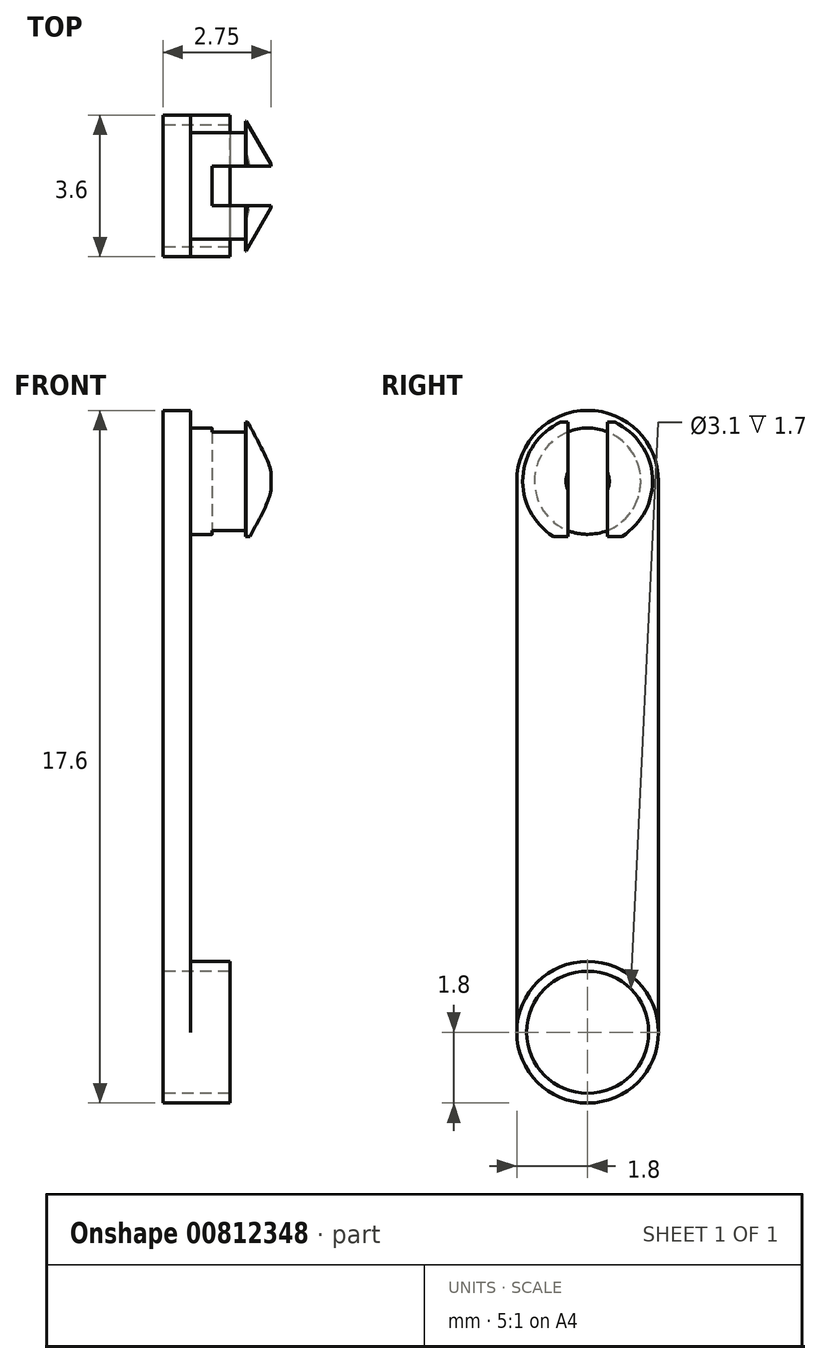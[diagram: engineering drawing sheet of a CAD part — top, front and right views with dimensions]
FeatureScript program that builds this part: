
annotation { "Feature Type Name" : "Feature", "Feature Type Description" : "" }
export const myFeature = defineFeature(function(context is Context, id is Id, definition is map)
    precondition{}
    {
        {
            var Q0;
            Q0=qCreatedBy(makeId("Right.planeOp"),FACE);
            var sketch = newSketch(context, id + "F0", { "sketchPlane" : qUnion([Q0])});
            skLineSegment(sketch, "E0.left", {"start": v(1.8, 7) * mm, "end": v(1.8, -7) * mm});
            skLineSegment(sketch, "E0.right", {"start": v(-1.8, 7) * mm, "end": v(-1.8, -7) * mm});
            skPoint(sketch, "E0.middle", {"position": v(0, 0) * mm});
            skArc(sketch, "E1", {"start": v(-1.8, 7) * mm, "mid": v(0, 8.8) * mm, "end": v(1.8, 7) * mm});
            skArc(sketch, "E2", {"start": v(-1.8, -7) * mm, "mid": v(0, -8.8) * mm, "end": v(1.8, -7) * mm});
            skCircle(sketch, "E3", {"center": v(0, -7) * mm, "radius": 1.55 * mm});
            skSolve(sketch);
        }
        {
            var Q0;
            Q0=makeQuery(id+"F0.imprint","IMPRINT",FACE,{"disambiguationData":[TD([[makeQuery(id+"F0.imprint","IMPRINT",EDGE,{"derivedFrom":sQuery(id+"F0.wireOp",EDGE,"E0.left")}),-1.0]])]});
            extrude(context, id + "F1", {"entities" : qUnion([Q0]), "depth" : .7 * mm, "offsetDistance" : 25 * mm});
        }
        {
            var Q0;
            Q0=makeQuery(id+"F1.opExtrude","CAP_FACE",FACE,{"disambiguationData":[OSD([sQuery(id+"F0.wireOp",EDGE,"E0.left"),sQuery(id+"F0.wireOp",EDGE,"E0.right"),sQuery(id+"F0.wireOp",EDGE,"E1"),sQuery(id+"F0.wireOp",EDGE,"E2"),sQuery(id+"F0.wireOp",EDGE,"E3")])],"isStart":false});
            var sketch = newSketch(context, id + "F2", { "sketchPlane" : qUnion([Q0])});
            skCircle(sketch, "E4", {"center": v(0, 7) * mm, "radius": 1.35 * mm});
            skSolve(sketch);
        }
        {
            var Q0;
            Q0=makeQuery(id+"F2.imprint","IMPRINT",FACE,{"disambiguationData":[TD([[makeQuery(id+"F2.imprint","IMPRINT",EDGE,{"derivedFrom":sQuery(id+"F2.wireOp",EDGE,"E4")}),1.0]])]});
            extrude(context, id + "F3", {"entities" : qUnion([Q0]), "operationType" : NewBodyOperationType.ADD, "depth" : 1.4 * mm, "offsetDistance" : 25 * mm});
        }
        {
            var Q0;
            Q0=makeQuery(id+"F3.opExtrude","CAP_FACE",FACE,{"disambiguationData":[OSD([sQuery(id+"F2.wireOp",EDGE,"E4")])],"isStart":false});
            var sketch = newSketch(context, id + "F4", { "sketchPlane" : qUnion([Q0])});
            skCircle(sketch, "E5", {"center": v(0, 7) * mm, "radius": 1.65 * mm});
            skSolve(sketch);
        }
        {
            var Q0;
            Q0 = qSketchRegion(id + "F4", true);
            extrude(context, id + "F5", {"entities" : qUnion([Q0]), "operationType" : NewBodyOperationType.ADD, "depth" : 0.65 * mm, "offsetDistance" : 25 * mm});
        }
        {
            var Q0;
            Q0=makeQuery(id+"F5.opExtrude","CAP_EDGE",EDGE,{"disambiguationData":[OSD([sQuery(id+"F4.wireOp",EDGE,"E5")])],"isStart":false});
            chamfer(context, id + "F6", {"entities" : qUnion([Q0]), "chamferType" : ChamferType.OFFSET_ANGLE, "width" : 1.1 * mm, "oppositeDirection" : false, "angle" : 30 * degree, "tangentPropagation" : true});
        }
        {
            var Q0;
            Q0=makeQuery(id+"F5.opExtrude","CAP_FACE",FACE,{"disambiguationData":[OSD([sQuery(id+"F4.wireOp",EDGE,"E5")])],"isStart":false});
            var sketch = newSketch(context, id + "F7", { "sketchPlane" : qUnion([Q0])});
            skLineSegment(sketch, "E6.bottom", {"start": v(-0.5, 8.8) * mm, "end": v(0.5, 8.8) * mm});
            skLineSegment(sketch, "E6.top", {"start": v(-0.5, 5.3) * mm, "end": v(0.5, 5.3) * mm});
            skLineSegment(sketch, "E6.left", {"start": v(-0.5, 8.5) * mm, "end": v(-0.5, 5.6) * mm});
            skLineSegment(sketch, "E6.right", {"start": v(0.5, 8.5) * mm, "end": v(0.5, 5.6) * mm});
            skLineSegment(sketch, "E7.bottom", {"start": v(-1, 8.8) * mm, "end": v(1, 8.8) * mm});
            skLineSegment(sketch, "E7.top", {"start": v(-1, 8.5) * mm, "end": v(-0.5, 8.5) * mm});
            skLineSegment(sketch, "E7.left", {"start": v(-1, 8.8) * mm, "end": v(-1, 8.5) * mm});
            skLineSegment(sketch, "E7.right", {"start": v(1, 8.8) * mm, "end": v(1, 8.5) * mm});
            skLineSegment(sketch, "E8.bottom", {"start": v(-1, 5.3) * mm, "end": v(1, 5.3) * mm});
            skLineSegment(sketch, "E8.top", {"start": v(-1, 5.6) * mm, "end": v(-0.5, 5.6) * mm});
            skLineSegment(sketch, "E8.left", {"start": v(-1, 5.3) * mm, "end": v(-1, 5.6) * mm});
            skLineSegment(sketch, "E8.right", {"start": v(1, 5.3) * mm, "end": v(1, 5.6) * mm});
            skLineSegment(sketch, "E9.trimOffspring", {"start": v(0.5, 8.5) * mm, "end": v(1, 8.5) * mm});
            skLineSegment(sketch, "E10.trimOffspring", {"start": v(0.5, 5.6) * mm, "end": v(1, 5.6) * mm});
            skSolve(sketch);
        }
        {
            var Q0;
            {var subQ0=sQuery(id+"F7.wireOp",EDGE,"E7.top");Q0=makeQuery(id+"F7.imprint","IMPRINT",FACE,{"disambiguationData":[TD([[makeQuery(id+"F7.imprint","IMPRINT",EDGE,{"derivedFrom":subQ0}),1.0]])]});}
            var Q1;
            {var subQ0=sQuery(id+"F7.wireOp",EDGE,"E6.left");var subQ1=sQuery(id+"F4.wireOp",EDGE,"E5");var subQ2=makeQuery(id+"F6.opChamfer","BLEND_EDGE",EDGE,{"blendedFrom":[makeQuery(id+"F5.opExtrude","CAP_EDGE",EDGE,{"disambiguationData":[OSD([subQ1])],"isStart":false}),makeQuery(id+"F5.opExtrude","CAP_FACE",FACE,{"disambiguationData":[OSD([subQ1])],"isStart":false})],"blendedInto":[makeQuery(id+"F5.opExtrude","CAP_FACE",FACE,{"disambiguationData":[OSD([subQ1])],"isStart":false})]});var subQ3=makeQuery(id+"F7.imprint","INTERSECT",VERTEX,{"disambiguationData":[OD(0.0)],"derivedFrom":[subQ2,subQ0]});Q1=makeQuery(id+"F7.imprint","IMPRINT",FACE,{"disambiguationData":[TD([[makeQuery(id+"F7.imprint","IMPRINT",EDGE,{"disambiguationData":[TD([[subQ3,-1.0]])],"derivedFrom":subQ0}),1.0]])]});}
            var Q2;
            {var subQ0=sQuery(id+"F7.wireOp",EDGE,"E8.top");Q2=makeQuery(id+"F7.imprint","IMPRINT",FACE,{"disambiguationData":[TD([[makeQuery(id+"F7.imprint","IMPRINT",EDGE,{"derivedFrom":subQ0}),-1.0]])]});}
            extrude(context, id + "F8", {"entities" : qUnion([Q0, Q1, Q2]), "operationType" : NewBodyOperationType.REMOVE, "oppositeDirection" : true, "depth" : 1.5 * mm, "offsetDistance" : 25 * mm});
        }
        {
            var Q0;
            Q0=makeQuery(id+"F1.opExtrude","CAP_FACE",FACE,{"disambiguationData":[OSD([sQuery(id+"F0.wireOp",EDGE,"E0.left"),sQuery(id+"F0.wireOp",EDGE,"E0.right"),sQuery(id+"F0.wireOp",EDGE,"E1"),sQuery(id+"F0.wireOp",EDGE,"E2"),sQuery(id+"F0.wireOp",EDGE,"E3")])],"isStart":false});
            var sketch = newSketch(context, id + "F9", { "sketchPlane" : qUnion([Q0])});
            skCircle(sketch, "E11", {"center": v(0, -7) * mm, "radius": 1.8 * mm});
            skCircle(sketch, "E12", {"center": v(0, -7) * mm, "radius": 1.55 * mm});
            skSolve(sketch);
        }
        {
            var Q0;
            Q0 = qSketchRegion(id + "F9", true);
            extrude(context, id + "F10", {"entities" : qUnion([Q0]), "operationType" : NewBodyOperationType.ADD, "depth" : 1 * mm, "offsetDistance" : 25 * mm});
        }
    });
